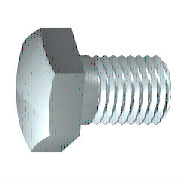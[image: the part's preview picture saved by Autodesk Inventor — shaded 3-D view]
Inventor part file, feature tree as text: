
AUTODESK INVENTOR PART (.ipt)
format: ipt  version: 2021 (Build 250183000, 183)  size: 193,536 bytes
history: native  units: mm (DEFAULTED — no unit token found)
features: sketch x3, extrude x1, chamfer x1, plane x1
ambient origin geometry x7: Origin, YZ Plane, XZ Plane, X Axis, Y Axis, Z Axis, Center Point
bodies: Solid1 (feature_tree), Body (feature_tree)
feature tree (6):
  extrude  "Head"  Depth=34.7mm
  chamfer  "Chamfer1"  Distance=6.9mm
  plane  "Work Plane1"
  sketch  "Sketch1"  dims[d0=40.0mm d1=34.7mm]
  sketch  "Sketch2"  dims[d2=12.0mm]
  sketch  "Sketch4"  dims[d12=90.0deg d3=6.9mm d4=0.0mm d5=30.0deg d21=90.0deg d6=1.073538mm d7=1.073638mm d8=0.0mm d9=0.6001mm d10=16.63mm d11=18.0mm d13=1.073638mm d14=12.0mm d15=34.7mm d16=0.0mm d19=18.0mm d55=45.0deg d57=0.0mm d58=0.0mm]
